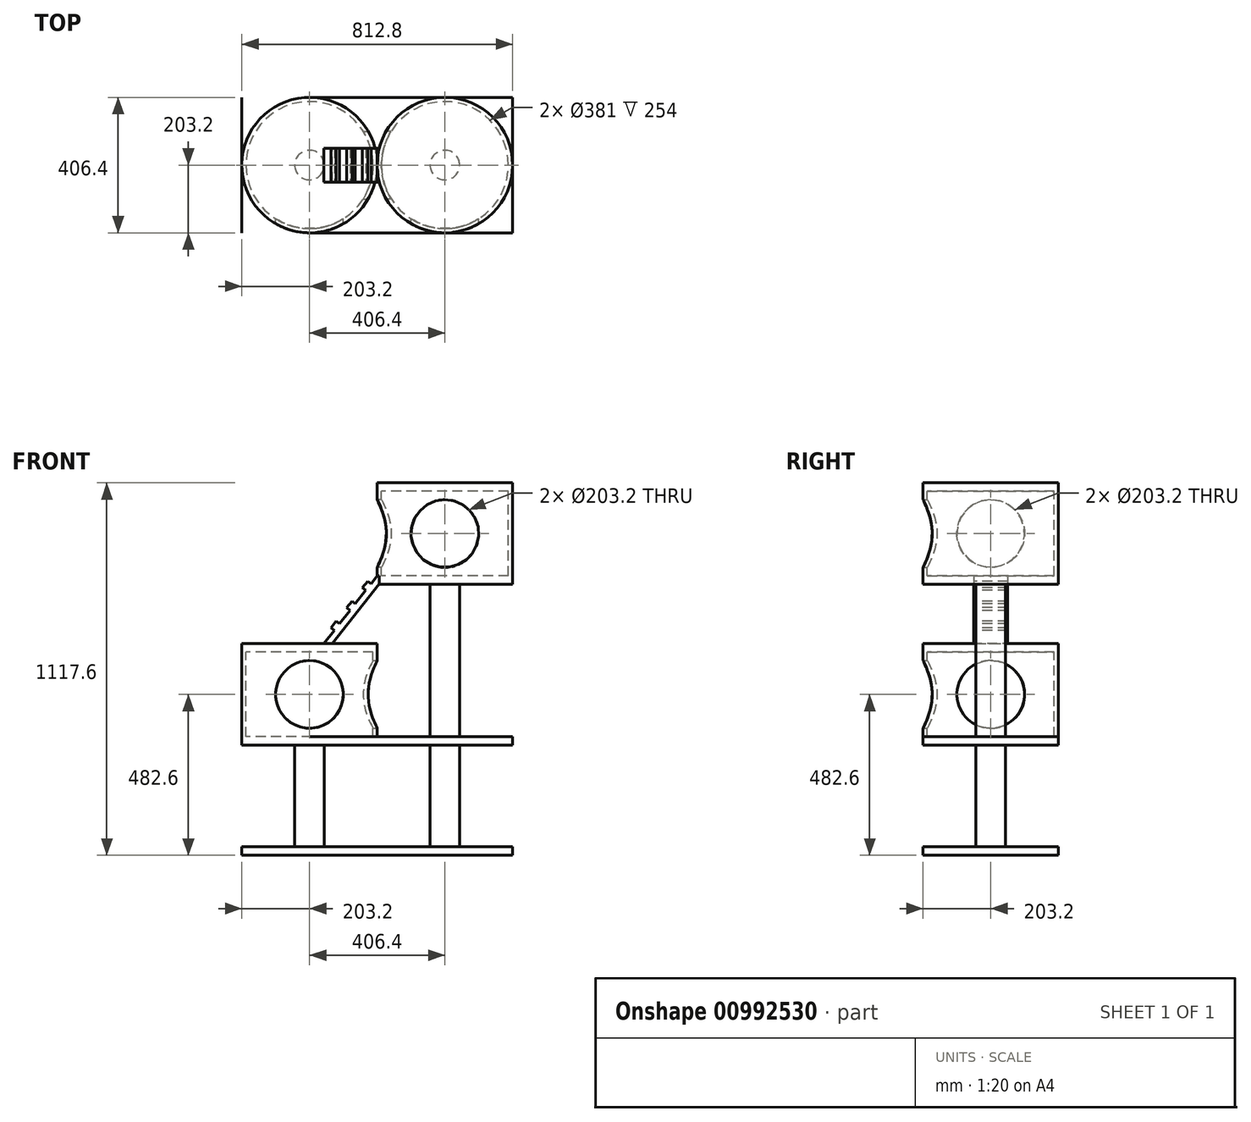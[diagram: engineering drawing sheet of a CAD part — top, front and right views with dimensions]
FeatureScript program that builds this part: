
annotation { "Feature Type Name" : "Feature", "Feature Type Description" : "" }
export const myFeature = defineFeature(function(context is Context, id is Id, definition is map)
    precondition{}
    {
        {
            var Q0;
            Q0=qCreatedBy(makeId("Top.planeOp"),FACE);
            var sketch = newSketch(context, id + "F0", { "sketchPlane" : qUnion([Q0])});
            skLineSegment(sketch, "E0", {"start": v(-203.2, 203.2) * mm, "end": v(406.4, 203.2) * mm});
            skLineSegment(sketch, "E1", {"start": v(406.4, 203.2) * mm, "end": v(406.4, -203.2) * mm});
            skLineSegment(sketch, "E2", {"start": v(406.4, -203.2) * mm, "end": v(-203.2, -203.2) * mm});
            skArc(sketch, "E3", {"start": v(-203.2, 203.2) * mm, "mid": v(-406.4, 0) * mm, "end": v(-203.2, -203.2) * mm});
            skSolve(sketch);
        }
        {
            var Q0;
            Q0=makeQuery(id+"F0.imprint","IMPRINT",FACE,{"disambiguationData":[TD([[makeQuery(id+"F0.imprint","IMPRINT",EDGE,{"derivedFrom":sQuery(id+"F0.wireOp",EDGE,"E0")}),-1.0]])]});
            extrude(context, id + "F1", {"entities" : qUnion([Q0]), "endBound" : BoundingType.SYMMETRIC, "depth" : 25.4 * mm, "offsetDistance" : 25.4 * mm});
        }
        {
            var Q0;
            Q0=makeQuery(id+"F1.opExtrude","CAP_FACE",FACE,{"disambiguationData":[OSD([sQuery(id+"F0.wireOp",EDGE,"E0"),sQuery(id+"F0.wireOp",EDGE,"E1"),sQuery(id+"F0.wireOp",EDGE,"E2"),sQuery(id+"F0.wireOp",EDGE,"E3")])],"isStart":true});
            var sketch = newSketch(context, id + "F2", { "sketchPlane" : qUnion([Q0])});
            skCircle(sketch, "E4", {"center": v(203.2, 0) * mm, "radius": 44.45 * mm});
            skCircle(sketch, "E5", {"center": v(-203.2, 0) * mm, "radius": 44.45 * mm});
            skSolve(sketch);
        }
        {
            var Q0;
            Q0=makeQuery(id+"F2.imprint","IMPRINT",FACE,{"disambiguationData":[TD([[makeQuery(id+"F2.imprint","IMPRINT",EDGE,{"derivedFrom":sQuery(id+"F2.wireOp",EDGE,"E5")}),1.0]])]});
            var Q1;
            Q1=makeQuery(id+"F2.imprint","IMPRINT",FACE,{"disambiguationData":[TD([[makeQuery(id+"F2.imprint","IMPRINT",EDGE,{"derivedFrom":sQuery(id+"F2.wireOp",EDGE,"E4")}),1.0]])]});
            extrude(context, id + "F3", {"entities" : qUnion([Q0, Q1]), "operationType" : NewBodyOperationType.ADD, "depth" : 304.8 * mm, "offsetDistance" : 25.4 * mm});
        }
        {
            var Q0;
            Q0=makeQuery(id+"F3.opExtrude","CAP_FACE",FACE,{"disambiguationData":[OSD([sQuery(id+"F2.wireOp",EDGE,"E4")])],"isStart":false});
            var sketch = newSketch(context, id + "F4", { "sketchPlane" : qUnion([Q0])});
            skLineSegment(sketch, "E6.bottom", {"start": v(-406.4, 203.2) * mm, "end": v(406.4, 203.2) * mm});
            skLineSegment(sketch, "E6.top", {"start": v(-406.4, -203.2) * mm, "end": v(406.4, -203.2) * mm});
            skLineSegment(sketch, "E6.left", {"start": v(-406.4, 203.2) * mm, "end": v(-406.4, -203.2) * mm});
            skLineSegment(sketch, "E6.right", {"start": v(406.4, 203.2) * mm, "end": v(406.4, -203.2) * mm});
            skSolve(sketch);
        }
        {
            var Q0;
            Q0 = qSketchRegion(id + "F4", true);
            extrude(context, id + "F5", {"entities" : qUnion([Q0]), "operationType" : NewBodyOperationType.ADD, "depth" : 25.4 * mm, "offsetDistance" : 25.4 * mm});
        }
        {
            var Q0;
            Q0=makeQuery(id+"F1.opExtrude","CAP_FACE",FACE,{"disambiguationData":[OSD([sQuery(id+"F0.wireOp",EDGE,"E0"),sQuery(id+"F0.wireOp",EDGE,"E1"),sQuery(id+"F0.wireOp",EDGE,"E2"),sQuery(id+"F0.wireOp",EDGE,"E3")])],"isStart":false});
            var sketch = newSketch(context, id + "F6", { "sketchPlane" : qUnion([Q0])});
            skCircle(sketch, "E7", {"center": v(-203.2, 0) * mm, "radius": 203.2 * mm});
            skSolve(sketch);
        }
        {
            var Q0;
            {var subQ0=sQuery(id+"F6.wireOp",EDGE,"E7");var subQ1=makeQuery(id+"F6.imprint","INTERSECT",VERTEX,{"derivedFrom":[makeQuery(id+"F1.opExtrude","CAP_EDGE",EDGE,{"disambiguationData":[OSD([sQuery(id+"F0.wireOp",EDGE,"E0")])],"isStart":false}),subQ0]});Q0=makeQuery(id+"F6.imprint","IMPRINT",FACE,{"disambiguationData":[TD([[makeQuery(id+"F6.imprint","IMPRINT",EDGE,{"disambiguationData":[TD([[subQ1,-1.0]])],"derivedFrom":subQ0}),1.0]])]});}
            extrude(context, id + "F7", {"entities" : qUnion([Q0]), "operationType" : NewBodyOperationType.ADD, "depth" : 254 * mm, "offsetDistance" : 25.4 * mm});
        }
        {
            var Q0;
            Q0=makeQuery(id+"F7.opExtrude","CAP_FACE",FACE,{"disambiguationData":[OSD([sQuery(id+"F6.wireOp",EDGE,"E7")])],"isStart":false});
            var sketch = newSketch(context, id + "F8", { "sketchPlane" : qUnion([Q0])});
            skPoint(sketch, "E8", {"position": v(-203.2, 0) * mm});
            skCircle(sketch, "E9", {"center": v(-203.2, 0) * mm, "radius": 190.5 * mm});
            skSolve(sketch);
        }
        {
            var Q0;
            Q0=makeQuery(id+"F8.imprint","IMPRINT",FACE,{"disambiguationData":[TD([[makeQuery(id+"F8.imprint","IMPRINT",EDGE,{"derivedFrom":sQuery(id+"F8.wireOp",EDGE,"E9")}),1.0]])]});
            extrude(context, id + "F9", {"entities" : qUnion([Q0]), "operationType" : NewBodyOperationType.REMOVE, "oppositeDirection" : true, "depth" : 254 * mm, "offsetDistance" : 25.4 * mm});
        }
        {
            var Q0;
            Q0=qCreatedBy(makeId("Right.planeOp"),FACE);
            var sketch = newSketch(context, id + "F10", { "sketchPlane" : qUnion([Q0])});
            skCircle(sketch, "E10", {"center": v(0, 139.7) * mm, "radius": 101.6 * mm});
            skLineSegment(sketch, "E11", {"start": v(-202.54, 0) * mm, "end": v(-202.54, 266.7) * mm, "construction": true});
            skSolve(sketch);
        }
        {
            var Q0;
            Q0=makeQuery(id+"F10.imprint","IMPRINT",FACE,{"disambiguationData":[TD([[makeQuery(id+"F10.imprint","IMPRINT",EDGE,{"derivedFrom":sQuery(id+"F10.wireOp",EDGE,"E10")}),1.0]])]});
            extrude(context, id + "F11", {"entities" : qUnion([Q0]), "operationType" : NewBodyOperationType.REMOVE, "oppositeDirection" : true, "depth" : 205.74 * mm, "offsetDistance" : 25.4 * mm});
        }
        {
            var Q0;
            Q0=qCreatedBy(makeId("Front.planeOp"),FACE);
            var sketch = newSketch(context, id + "F12", { "sketchPlane" : qUnion([Q0])});
            skCircle(sketch, "E12", {"center": v(-203.2, 139.7) * mm, "radius": 101.6 * mm});
            skSolve(sketch);
        }
        {
            var Q0;
            Q0 = qSketchRegion(id + "F12", true);
            extrude(context, id + "F13", {"entities" : qUnion([Q0]), "operationType" : NewBodyOperationType.REMOVE, "depth" : 350.52 * mm, "offsetDistance" : 25.4 * mm});
        }
        {
            var Q0;
            Q0=makeQuery(id+"F7.opExtrude","CAP_FACE",FACE,{"disambiguationData":[OSD([sQuery(id+"F6.wireOp",EDGE,"E7")])],"isStart":false});
            var sketch = newSketch(context, id + "F14", { "sketchPlane" : qUnion([Q0])});
            skCircle(sketch, "E13", {"center": v(-203.2, 0) * mm, "radius": 203.2 * mm});
            skSolve(sketch);
        }
        {
            var Q0;
            Q0 = qSketchRegion(id + "F14", true);
            extrude(context, id + "F15", {"entities" : qUnion([Q0]), "operationType" : NewBodyOperationType.ADD, "depth" : 25.4 * mm, "offsetDistance" : 25.4 * mm});
        }
        {
            var Q0;
            Q0=makeQuery(id+"F1.opExtrude","CAP_FACE",FACE,{"disambiguationData":[OSD([sQuery(id+"F0.wireOp",EDGE,"E0"),sQuery(id+"F0.wireOp",EDGE,"E1"),sQuery(id+"F0.wireOp",EDGE,"E2"),sQuery(id+"F0.wireOp",EDGE,"E3")])],"isStart":false});
            var sketch = newSketch(context, id + "F16", { "sketchPlane" : qUnion([Q0])});
            skCircle(sketch, "E14", {"center": v(203.2, 0) * mm, "radius": 44.45 * mm});
            skSolve(sketch);
        }
        {
            var Q0;
            Q0=makeQuery(id+"F16.imprint","IMPRINT",FACE,{"disambiguationData":[TD([[makeQuery(id+"F16.imprint","IMPRINT",EDGE,{"derivedFrom":sQuery(id+"F16.wireOp",EDGE,"E14")}),1.0]])]});
            extrude(context, id + "F17", {"entities" : qUnion([Q0]), "operationType" : NewBodyOperationType.ADD, "depth" : 457.2 * mm, "offsetDistance" : 25.4 * mm});
        }
        {
            var Q0;
            Q0=makeQuery(id+"F17.opExtrude","CAP_FACE",FACE,{"disambiguationData":[OSD([sQuery(id+"F16.wireOp",EDGE,"E14")])],"isStart":false});
            var sketch = newSketch(context, id + "F18", { "sketchPlane" : qUnion([Q0])});
            skCircle(sketch, "E15", {"center": v(203.2, 0) * mm, "radius": 203.2 * mm});
            skSolve(sketch);
        }
        {
            var Q0;
            Q0=makeQuery(id+"F18.imprint","IMPRINT",FACE,{"disambiguationData":[TD([[makeQuery(id+"F18.imprint","IMPRINT",EDGE,{"derivedFrom":makeQuery(id+"F17.opExtrude","CAP_EDGE",EDGE,{"disambiguationData":[OSD([sQuery(id+"F16.wireOp",EDGE,"E14")])],"isStart":false})}),1.0]])]});
            var Q1;
            Q1=makeQuery(id+"F18.imprint","IMPRINT",FACE,{"disambiguationData":[TD([[makeQuery(id+"F18.imprint","IMPRINT",EDGE,{"derivedFrom":sQuery(id+"F18.wireOp",EDGE,"E15")}),1.0]])]});
            extrude(context, id + "F19", {"entities" : qUnion([Q0, Q1]), "operationType" : NewBodyOperationType.ADD, "depth" : 279.4 * mm, "offsetDistance" : 25.4 * mm});
        }
        {
            var Q0;
            Q0=makeQuery(id+"F19.opExtrude","CAP_FACE",FACE,{"disambiguationData":[OSD([sQuery(id+"F18.wireOp",EDGE,"E15")])],"isStart":false});
            var sketch = newSketch(context, id + "F20", { "sketchPlane" : qUnion([Q0])});
            skCircle(sketch, "E16", {"center": v(203.2, 0) * mm, "radius": 190.5 * mm});
            skSolve(sketch);
        }
        {
            var Q0;
            Q0=makeQuery(id+"F20.imprint","IMPRINT",FACE,{"disambiguationData":[TD([[makeQuery(id+"F20.imprint","IMPRINT",EDGE,{"derivedFrom":sQuery(id+"F20.wireOp",EDGE,"E16")}),1.0]])]});
            var Q1;
            Q1=sQuery(id+"F20.wireOp",EDGE,"E16");
            extrude(context, id + "F21", {"entities" : qUnion([Q0]), "operationType" : NewBodyOperationType.REMOVE, "surfaceEntities" : qUnion([Q1]), "oppositeDirection" : true, "depth" : 254 * mm, "offsetDistance" : 25.4 * mm});
        }
        {
            var Q0;
            Q0=qCreatedBy(makeId("Right.planeOp"),FACE);
            var sketch = newSketch(context, id + "F22", { "sketchPlane" : qUnion([Q0])});
            skCircle(sketch, "E17", {"center": v(0, 622.3) * mm, "radius": 101.6 * mm});
            skSolve(sketch);
        }
        {
            var Q0;
            Q0=makeQuery(id+"F22.imprint","IMPRINT",FACE,{"disambiguationData":[TD([[makeQuery(id+"F22.imprint","IMPRINT",EDGE,{"derivedFrom":sQuery(id+"F22.wireOp",EDGE,"E17")}),1.0]])]});
            extrude(context, id + "F23", {"entities" : qUnion([Q0]), "operationType" : NewBodyOperationType.REMOVE, "depth" : 218.44 * mm, "offsetDistance" : 25.4 * mm});
        }
        {
            var Q0;
            Q0=qCreatedBy(makeId("Front.planeOp"),FACE);
            var sketch = newSketch(context, id + "F24", { "sketchPlane" : qUnion([Q0])});
            skCircle(sketch, "E18", {"center": v(203.2, 622.3) * mm, "radius": 101.6 * mm});
            skLineSegment(sketch, "E19", {"start": v(0, 0) * mm, "end": v(0, 749.3) * mm, "construction": true});
            skSolve(sketch);
        }
        {
            var Q0;
            Q0=makeQuery(id+"F24.imprint","IMPRINT",FACE,{"disambiguationData":[TD([[makeQuery(id+"F24.imprint","IMPRINT",EDGE,{"derivedFrom":sQuery(id+"F24.wireOp",EDGE,"E18")}),1.0]])]});
            extrude(context, id + "F25", {"entities" : qUnion([Q0]), "operationType" : NewBodyOperationType.REMOVE, "depth" : 393.7 * mm, "offsetDistance" : 25.4 * mm});
        }
        {
            var Q0;
            Q0=makeQuery(id+"F19.opExtrude","CAP_FACE",FACE,{"disambiguationData":[OSD([sQuery(id+"F18.wireOp",EDGE,"E15")])],"isStart":false});
            var sketch = newSketch(context, id + "F26", { "sketchPlane" : qUnion([Q0])});
            skCircle(sketch, "E20", {"center": v(203.2, 0) * mm, "radius": 203.2 * mm});
            skSolve(sketch);
        }
        {
            var Q0;
            Q0 = qSketchRegion(id + "F26", true);
            extrude(context, id + "F27", {"entities" : qUnion([Q0]), "operationType" : NewBodyOperationType.ADD, "depth" : 25.4 * mm, "offsetDistance" : 25.4 * mm});
        }
        {
            var Q0;
            Q0=qCreatedBy(makeId("Front.planeOp"),FACE);
            var sketch = newSketch(context, id + "F28", { "sketchPlane" : qUnion([Q0])});
            skLineSegment(sketch, "E21", {"start": v(0, 495.3) * mm, "end": v(-159.98, 292.1) * mm});
            skLineSegment(sketch, "E22", {"start": v(25.4, 495.3) * mm, "end": v(-134.58, 292.1) * mm});
            skLineSegment(sketch, "E23", {"start": v(-159.98, 292.1) * mm, "end": v(-134.58, 292.1) * mm});
            skLineSegment(sketch, "E24", {"start": v(25.4, 495.3) * mm, "end": v(0, 495.3) * mm});
            skSolve(sketch);
        }
        {
            var Q0;
            Q0=makeQuery(id+"F28.imprint","IMPRINT",FACE,{"disambiguationData":[TD([[makeQuery(id+"F28.imprint","IMPRINT",EDGE,{"derivedFrom":sQuery(id+"F28.wireOp",EDGE,"E21")}),1.0]])]});
            extrude(context, id + "F29", {"entities" : qUnion([Q0]), "operationType" : NewBodyOperationType.ADD, "endBound" : BoundingType.SYMMETRIC, "depth" : 101.6 * mm, "offsetDistance" : 25.4 * mm});
        }
        {
            var Q0;
            Q0=makeQuery(id+"F29.opExtrude","SWEPT_FACE",FACE,{"disambiguationData":[OSD([sQuery(id+"F28.wireOp",EDGE,"E21")])]});
            var sketch = newSketch(context, id + "F30", { "sketchPlane" : qUnion([Q0])});
            skLineSegment(sketch, "E25", {"start": v(-50.8, 130.55) * mm, "end": v(50.8, 130.55) * mm, "construction": true});
            skLineSegment(sketch, "E26.bottom", {"start": v(-50.8, 181.35) * mm, "end": v(50.8, 181.35) * mm});
            skLineSegment(sketch, "E26.top", {"start": v(-50.8, 206.75) * mm, "end": v(50.8, 206.75) * mm});
            skLineSegment(sketch, "E26.left", {"start": v(-50.8, 181.35) * mm, "end": v(-50.8, 206.75) * mm});
            skLineSegment(sketch, "E26.right", {"start": v(50.8, 181.35) * mm, "end": v(50.8, 206.75) * mm});
            skLineSegment(sketch, "E27.bottom", {"start": v(-50.8, 257.55) * mm, "end": v(50.8, 257.55) * mm});
            skLineSegment(sketch, "E27.top", {"start": v(-50.8, 282.95) * mm, "end": v(50.8, 282.95) * mm});
            skLineSegment(sketch, "E27.left", {"start": v(-50.8, 257.55) * mm, "end": v(-50.8, 282.95) * mm});
            skLineSegment(sketch, "E27.right", {"start": v(50.8, 257.55) * mm, "end": v(50.8, 282.95) * mm});
            skLineSegment(sketch, "E28.bottom", {"start": v(-50.8, 359.15) * mm, "end": v(50.8, 359.15) * mm});
            skLineSegment(sketch, "E28.top", {"start": v(-50.8, 333.75) * mm, "end": v(50.8, 333.75) * mm});
            skLineSegment(sketch, "E28.left", {"start": v(-50.8, 359.15) * mm, "end": v(-50.8, 333.75) * mm});
            skLineSegment(sketch, "E28.right", {"start": v(50.8, 359.15) * mm, "end": v(50.8, 333.75) * mm});
            skSolve(sketch);
        }
        {
            var Q0;
            Q0=makeQuery(id+"F30.imprint","IMPRINT",FACE,{"disambiguationData":[TD([[makeQuery(id+"F30.imprint","IMPRINT",EDGE,{"derivedFrom":sQuery(id+"F30.wireOp",EDGE,"E26.bottom")}),1.0]])]});
            var Q1;
            Q1=makeQuery(id+"F30.imprint","IMPRINT",FACE,{"disambiguationData":[TD([[makeQuery(id+"F30.imprint","IMPRINT",EDGE,{"derivedFrom":sQuery(id+"F30.wireOp",EDGE,"E27.bottom")}),1.0]])]});
            var Q2;
            Q2=makeQuery(id+"F30.imprint","IMPRINT",FACE,{"disambiguationData":[TD([[makeQuery(id+"F30.imprint","IMPRINT",EDGE,{"derivedFrom":sQuery(id+"F30.wireOp",EDGE,"E28.bottom")}),-1.0]])]});
            extrude(context, id + "F31", {"entities" : qUnion([Q0, Q1, Q2]), "operationType" : NewBodyOperationType.ADD, "depth" : 12.7 * mm, "offsetDistance" : 25.4 * mm});
        }
    });
